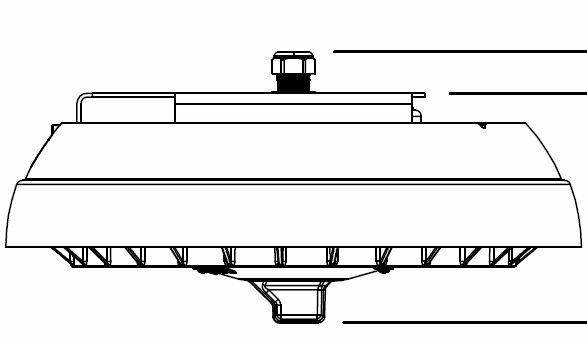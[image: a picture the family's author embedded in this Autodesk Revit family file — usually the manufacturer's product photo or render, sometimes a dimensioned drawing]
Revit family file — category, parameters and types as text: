
# Revit family: MET30
name_source: partatom
category: Lighting Fixtures
units: mm (PartAtom-declared; Revit-internal decimal feet)

## family parameters
Cut with Voids When Loaded = No
Host = Face
Light Source = Yes
OmniClass Number = 23.80.70.14.21
OmniClass Title = Street and Roadway Lighting
Part Type = Normal
Room Calculation Point = No
Round Connector Dimension = Use Diameter
Shared = No

## types (12) — shared parameters
Apparent Load = 0 VA
Color Filter = 16777215
Default Elevation = 48"
Description = 30” Metropolis Luminaire
Dimming Lamp Color Temperature Shift = <None>
Lamp = LED
Light Bulb Material = Glass
Manufacturer = Beacon Products
Model = Metropolis
Photometric Web File = generic
Tilt Angle = -90.00°
URL = https://www.currentlighting.com
Voltage = 120 V
Wattage Comments = 55-136 W
Watts = 136 W

## per-type parameters (varying)
| type | Finish |
| Basic Black Textured | Paint - Basic Black Textured |
| Black Matte Textured | Paint -Black Matte Textured |
| Bronze Textured | Paint -  Bronze Textured |
| Dark Bronze Textured | Paint - Dark Bronze Textured |
| Dark Platinum Smooth | Paint - Dark Platinum Smooth |
| Gray Smooth | Paint - Gray Smooth |
| Green Textured | Paint - Green Textured |
| Metallic Bronze Textured | Paint -  Metallic Bronze Textured |
| Metallic Silver Textured | Paint - Metallic Silver Textured |
| Metallic Titanium Textured | Paint -  Metallic Titanium Textured |
| Old World Iron | Paint - Old World Iron |
| White Texture | Paint -  White Texture |

## geometry (parser evidence)
native form markers: Blend x3, Sweep x5
no freeform markers — native parametric forms only
